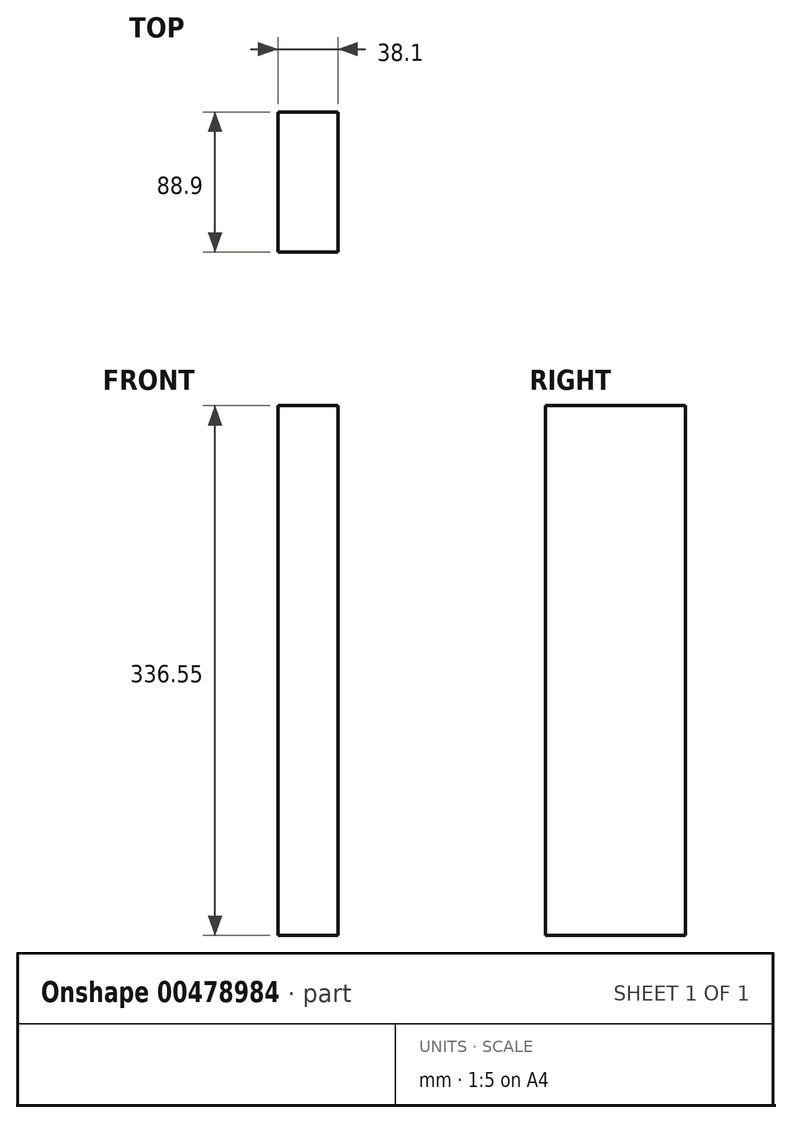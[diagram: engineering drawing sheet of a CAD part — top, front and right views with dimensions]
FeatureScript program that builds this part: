
annotation { "Feature Type Name" : "Feature", "Feature Type Description" : "" }
export const myFeature = defineFeature(function(context is Context, id is Id, definition is map)
    precondition{}
    {
        {
            var Q0;
            Q0=qCreatedBy(makeId("Front.planeOp"),FACE);
            var sketch = newSketch(context, id + "F0", { "sketchPlane" : qUnion([Q0])});
            skLineSegment(sketch, "E0.bottom", {"start": v(0, 0) * mm, "end": v(38.1, 0) * mm});
            skLineSegment(sketch, "E0.top", {"start": v(0, 336.55) * mm, "end": v(38.1, 336.55) * mm});
            skLineSegment(sketch, "E0.left", {"start": v(0, 0) * mm, "end": v(0, 336.55) * mm});
            skLineSegment(sketch, "E0.right", {"start": v(38.1, 0) * mm, "end": v(38.1, 336.55) * mm});
            skSolve(sketch);
        }
        {
            var Q0;
            Q0 = qSketchRegion(id + "F0", true);
            extrude(context, id + "F1", {"entities" : qUnion([Q0]), "depth" : 88.9 * mm});
        }
    });
